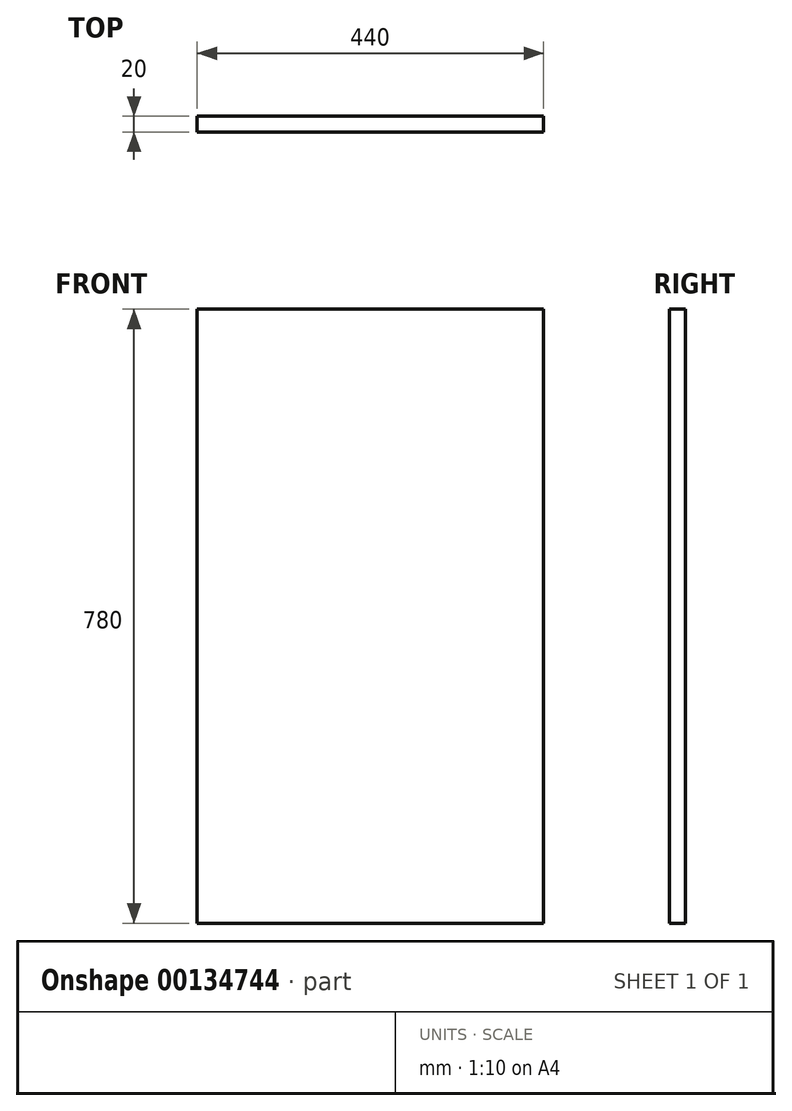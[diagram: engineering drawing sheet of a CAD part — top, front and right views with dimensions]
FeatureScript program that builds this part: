
annotation { "Feature Type Name" : "Feature", "Feature Type Description" : "" }
export const myFeature = defineFeature(function(context is Context, id is Id, definition is map)
    precondition{}
    {
        {
            var Q0;
            Q0=qCreatedBy(makeId("Front.planeOp"),FACE);
            var sketch = newSketch(context, id + "F0", { "sketchPlane" : qUnion([Q0])});
            skLineSegment(sketch, "E0.bottom", {"start": v(-247.06, 1.73) * mm, "end": v(192.94, 1.73) * mm});
            skLineSegment(sketch, "E0.top", {"start": v(-247.06, 781.73) * mm, "end": v(192.94, 781.73) * mm});
            skLineSegment(sketch, "E0.left", {"start": v(-247.06, 1.73) * mm, "end": v(-247.06, 781.73) * mm});
            skLineSegment(sketch, "E0.right", {"start": v(192.94, 1.73) * mm, "end": v(192.94, 781.73) * mm});
            skSolve(sketch);
        }
        {
            var Q0;
            Q0 = qSketchRegion(id + "F0", true);
            extrude(context, id + "F1", {"entities" : qUnion([Q0]), "depth" : 20 * mm});
        }
    });
